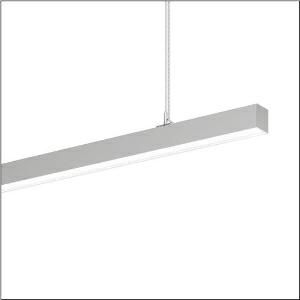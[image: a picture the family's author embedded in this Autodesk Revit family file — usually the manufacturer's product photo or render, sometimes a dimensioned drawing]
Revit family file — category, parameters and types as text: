
# Revit family: silica_r__21_51mx30da34sb_350b
name_source: partatom
category: Lighting Fixtures
units: mm (PartAtom-declared; Revit-internal decimal feet)

## family parameters
Cut with Voids When Loaded = No
Host = Face
Light Source = No
Part Type = Normal
Room Calculation Point = No
Round Connector Dimension = Use Diameter
Shared = No

## types (1)
- --- (1 x LED, 4210 lm, 27.7 W, 3000K)
    Apparent Load = 28 VA
    CIE Flux Codes = 47 79 96 57 100
    Color Rendering = 80
    Color Temperature = 3000K
    Default Elevation = 1800 mm
    Description = Silica® 21, office luminaire, primary optical cover: cover, of PMMA, opal, light emission: direct/indirect distribution, primary light characteristic: symmetric, installation type: suspended mounting, LED, rated luminous flux: 4.210lm, luminous efficacy: 152lm/W, light colour: 830, colour temperature: 3000K, with terminal, 3+2-pole, max. 2.5mm², mains connection: 220..240V, AC, 50/60Hz, rated input power: 27.7W, luminaire housing, of aluminium, metallic grey (RAL 9006), length: 1.204mm, width: 53mm, height: 53mm, protection rating (complete): IP20, insulation class (complete): insulation class I (protective earthing), certification: CE, permissible operating ambient temperature: 0..+35°C, standard: EN 50419, packaging unit: 1 piece
    Height = 53 mm
    Lamp = 1 x LED
    Lamp Light Flux = 4210 lm
    Lamp Power = 27.7 W
    Lamp count = 1
    Length = 1204 mm
    Luminous efficacy = 152 lm/W
    Manufacturer = Siteco
    ModVariant = No
    Model = 51MX30DA34SB
    Mounting Place = Ceiling
    Mounting Type = Pendant
    Number of Poles = 1
    OnlyDefault = Yes
    Power Factor = 1
    Product Name = Silica® 21
    Product group = office luminaire | ceiling pendant
    ProductGroupID = 902
    Protection Class = Protection class I
    Protection Degree = IP 20
    RLX_Detail_Level = 1
    RLX_Emergency_Light_Flux = 0 lm
    RLX_Emergency_Type = 0
    RLX_Emergency_Type_DB = No
    RlxData = <blob elided: 23189 chars, md5=cc0b802f>
    Socket = socket
    Standby Power = 0 W
    System Light Flux = 4210 lm
    System Power = 28 W
    Type Comments = factory setting: luminous flux: 100 % | dim-lin: 254 | 233 mA
    Type Image = l_1297747.jpg
    URL = http://relux.com
    VarID = @adj_047185
    Voltage = 0 V
    Weight = 0.00 kg
    Width = 53 mm

## geometry (parser evidence)
native form markers: Blend x4, Sweep x11
no freeform markers — native parametric forms only
